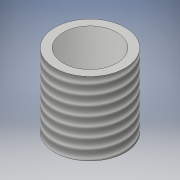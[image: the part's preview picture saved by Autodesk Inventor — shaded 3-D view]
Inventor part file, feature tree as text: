
AUTODESK INVENTOR PART (.ipt)
format: ipt  version: 2019.4 (Build 234330000, 330)  size: 114,176 bytes
history: native  units: in
note: dims shown in document units (in); Inventor stores cm internally (conversion verified against a paired STEP export)
features: extrude x2, sketch x2, thread x1
ambient origin geometry x8: Origin, YZ Plane, XZ Plane, XY Plane, X Axis, Y Axis, Z Axis, Center Point
bodies: Solid1 (feature_tree)
feature tree (5):
  extrude  "Extrusion1"  Depth=0.78in TaperAngle=0.0deg
  extrude  "Extrusion2"  Depth=1.23in TaperAngle=0.0deg
  thread  "Thread1"  [1 undecoded]
  sketch  "Sketch1"  dims[d0=0.75in d1=0.78in d2=0.0in]
  sketch  "Sketch2"  dims[d3=0.57in d4=1.23in d5=0.0in d6=1.0in d7=0.0in]
note: 1 required parameter value undecoded (feature->parameter linkage not recoverable at this tier; creation-order binding heuristic only, values carry confidence <= 0.55)
